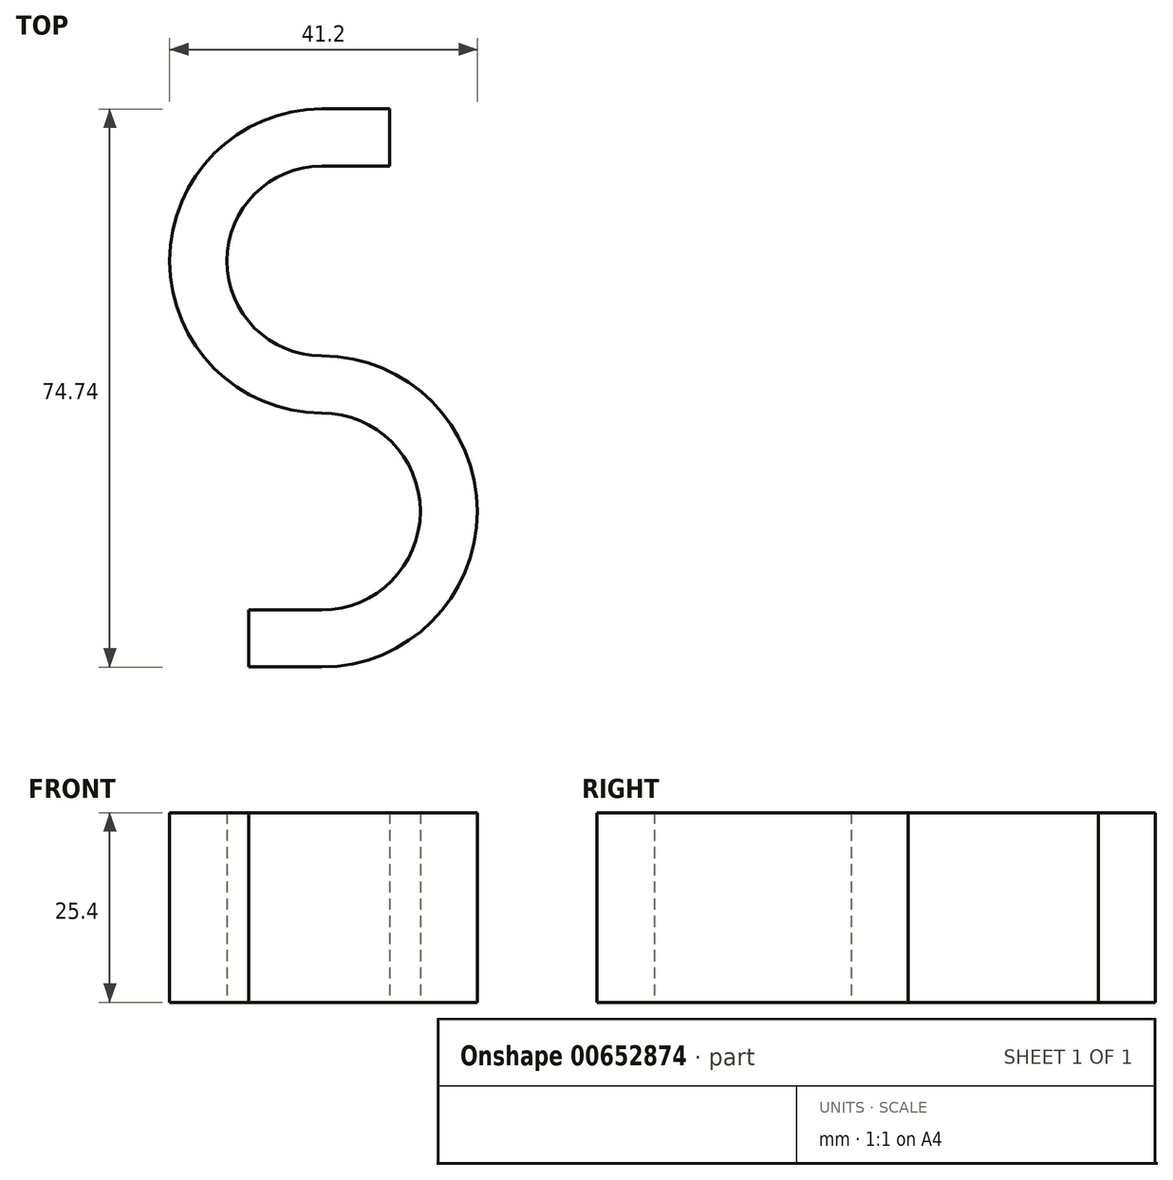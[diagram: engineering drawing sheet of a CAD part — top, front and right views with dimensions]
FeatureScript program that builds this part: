
annotation { "Feature Type Name" : "Feature", "Feature Type Description" : "" }
export const myFeature = defineFeature(function(context is Context, id is Id, definition is map)
    precondition{}
    {
        {
            var Q0;
            Q0=qCreatedBy(makeId("Top.planeOp"),FACE);
            var sketch = newSketch(context, id + "F0", { "sketchPlane" : qUnion([Q0])});
            skArc(sketch, "E0", {"start": v(0, -13.2) * mm, "mid": v(13.2, 0) * mm, "end": v(0, 13.2) * mm});
            skArc(sketch, "E1", {"start": v(0, 53.9) * mm, "mid": v(-20.36, 33.55) * mm, "end": v(0, 13.2) * mm});
            skArc(sketch, "E2", {"start": v(0, -20.84) * mm, "mid": v(20.84, 0) * mm, "end": v(0, 20.84) * mm});
            skArc(sketch, "E3", {"start": v(0, 46.25) * mm, "mid": v(-12.7, 33.55) * mm, "end": v(0, 20.84) * mm});
            skLineSegment(sketch, "E4", {"start": v(0, 53.9) * mm, "end": v(9.05, 53.9) * mm});
            skLineSegment(sketch, "E5", {"start": v(0, 46.25) * mm, "end": v(9.05, 46.25) * mm});
            skLineSegment(sketch, "E6", {"start": v(9.05, 53.9) * mm, "end": v(9.05, 46.25) * mm});
            skLineSegment(sketch, "E7", {"start": v(0, -20.84) * mm, "end": v(-9.77, -20.84) * mm});
            skLineSegment(sketch, "E8", {"start": v(0, -13.2) * mm, "end": v(-9.77, -13.2) * mm});
            skLineSegment(sketch, "E9", {"start": v(-9.77, -13.2) * mm, "end": v(-9.77, -20.84) * mm});
            skLineSegment(sketch, "E10", {"start": v(-9.77, -20.84) * mm, "end": v(-19.75, -20.84) * mm});
            skPoint(sketch, "E11.endSnap0", {"position": v(-18.86, -17.01) * mm});
            skLineSegment(sketch, "E12", {"start": v(-15.7, -20.84) * mm, "end": v(-14.76, -24) * mm});
            skPoint(sketch, "E12.endSnap0", {"position": v(-14.76, -20.84) * mm});
            skPoint(sketch, "E11.end.orphan", {"position": v(-18.86, -20.84) * mm});
            skPoint(sketch, "E13.end.orphan", {"position": v(-17.97, -13.2) * mm});
            skSolve(sketch);
        }
        {
            var Q0;
            Q0=makeQuery(id+"F0.imprint","IMPRINT",FACE,{"disambiguationData":[TD([[makeQuery(id+"F0.imprint","IMPRINT",EDGE,{"derivedFrom":sQuery(id+"F0.wireOp",EDGE,"E0")}),-1.0]])]});
            extrude(context, id + "F1", {"entities" : qUnion([Q0]), "depth" : 25.4 * mm, "offsetDistance" : 25.4 * mm});
        }
    });
